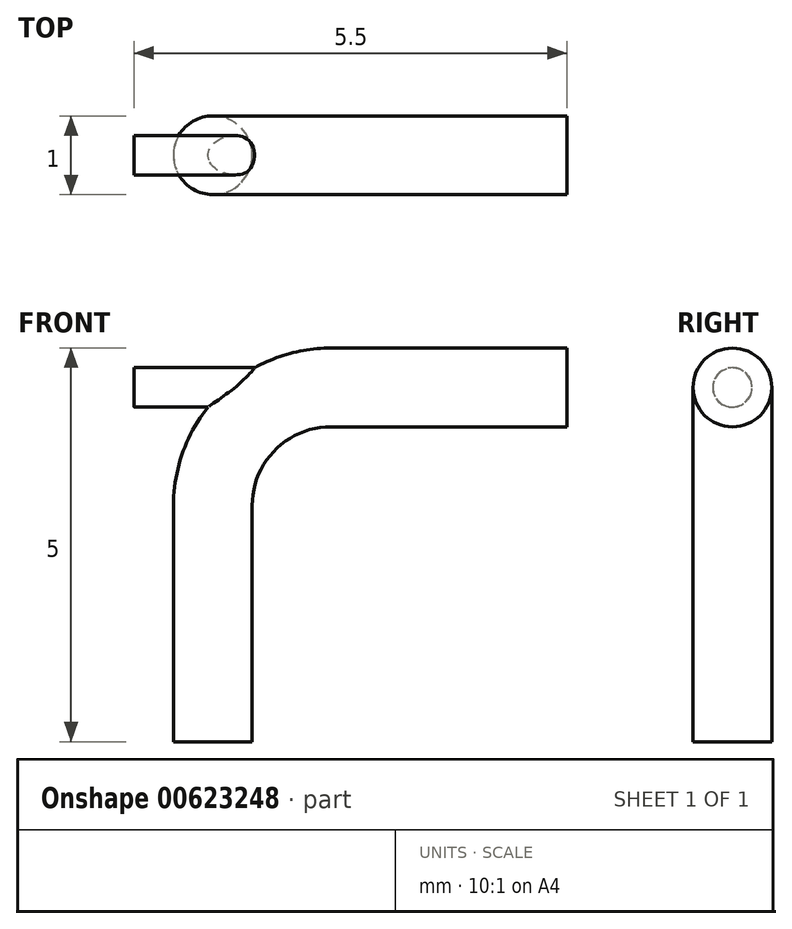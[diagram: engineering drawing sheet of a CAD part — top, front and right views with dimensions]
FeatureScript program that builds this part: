
annotation { "Feature Type Name" : "Feature", "Feature Type Description" : "" }
export const myFeature = defineFeature(function(context is Context, id is Id, definition is map)
    precondition{}
    {
        {
            var Q0;
            Q0=qCreatedBy(makeId("Front.planeOp"),FACE);
            var sketch = newSketch(context, id + "F0", { "sketchPlane" : qUnion([Q0])});
            skLineSegment(sketch, "E0", {"start": v(0, 0) * mm, "end": v(0, 3) * mm});
            skArc(sketch, "E1", {"start": v(1.5, 4.5) * mm, "mid": v(0.44, 4.06) * mm, "end": v(0, 3) * mm});
            skLineSegment(sketch, "E2", {"start": v(1.5, 4.5) * mm, "end": v(4.5, 4.5) * mm});
            skSolve(sketch);
        }
        {
            var Q0;
            Q0=qCreatedBy(makeId("Top.planeOp"),FACE);
            var sketch = newSketch(context, id + "F1", { "sketchPlane" : qUnion([Q0])});
            skCircle(sketch, "E3", {"center": v(0, 0) * mm, "radius": 0.5 * mm});
            skSolve(sketch);
        }
        {
            var Q0;
            Q0=makeQuery(id+"F1.imprint","IMPRINT",FACE,{"disambiguationData":[TD([[makeQuery(id+"F1.imprint","IMPRINT",EDGE,{"derivedFrom":sQuery(id+"F1.wireOp",EDGE,"E3")}),1.0]])]});
            var Q1;
            Q1 = qConstructionFilter(qBodyType(qCreatedBy(id + "F0" ,EDGE), BodyType.WIRE), ConstructionObject.NO);
            sweep(context, id + "F2", {"profiles" : qUnion([Q0]), "path" : qUnion([Q1])});
        }
        {
            var Q0;
            Q0=qCreatedBy(makeId("Right.planeOp"),FACE);
            cPlane(context, id + "F3", {"entities" : qUnion([Q0]), "cplaneType" : CPlaneType.OFFSET, "offset" : 1 * mm, "oppositeDirection" : true, "width" : 150 * mm, "height" : 150 * mm});
        }
        {
            var Q0;
            Q0=qCreatedBy(id+"F3.planeOp",FACE);
            var sketch = newSketch(context, id + "F4", { "sketchPlane" : qUnion([Q0])});
            skCircle(sketch, "E4", {"center": v(0, 4.5) * mm, "radius": 0.25 * mm});
            skSolve(sketch);
        }
        {
            var Q0;
            Q0=makeQuery(id+"F4.imprint","IMPRINT",FACE,{"disambiguationData":[TD([[makeQuery(id+"F4.imprint","IMPRINT",EDGE,{"derivedFrom":sQuery(id+"F4.wireOp",EDGE,"E4")}),1.0]])]});
            extrude(context, id + "F5", {"entities" : qUnion([Q0]), "operationType" : NewBodyOperationType.ADD, "depth" : 3 * mm, "offsetDistance" : 25 * mm});
        }
    });
